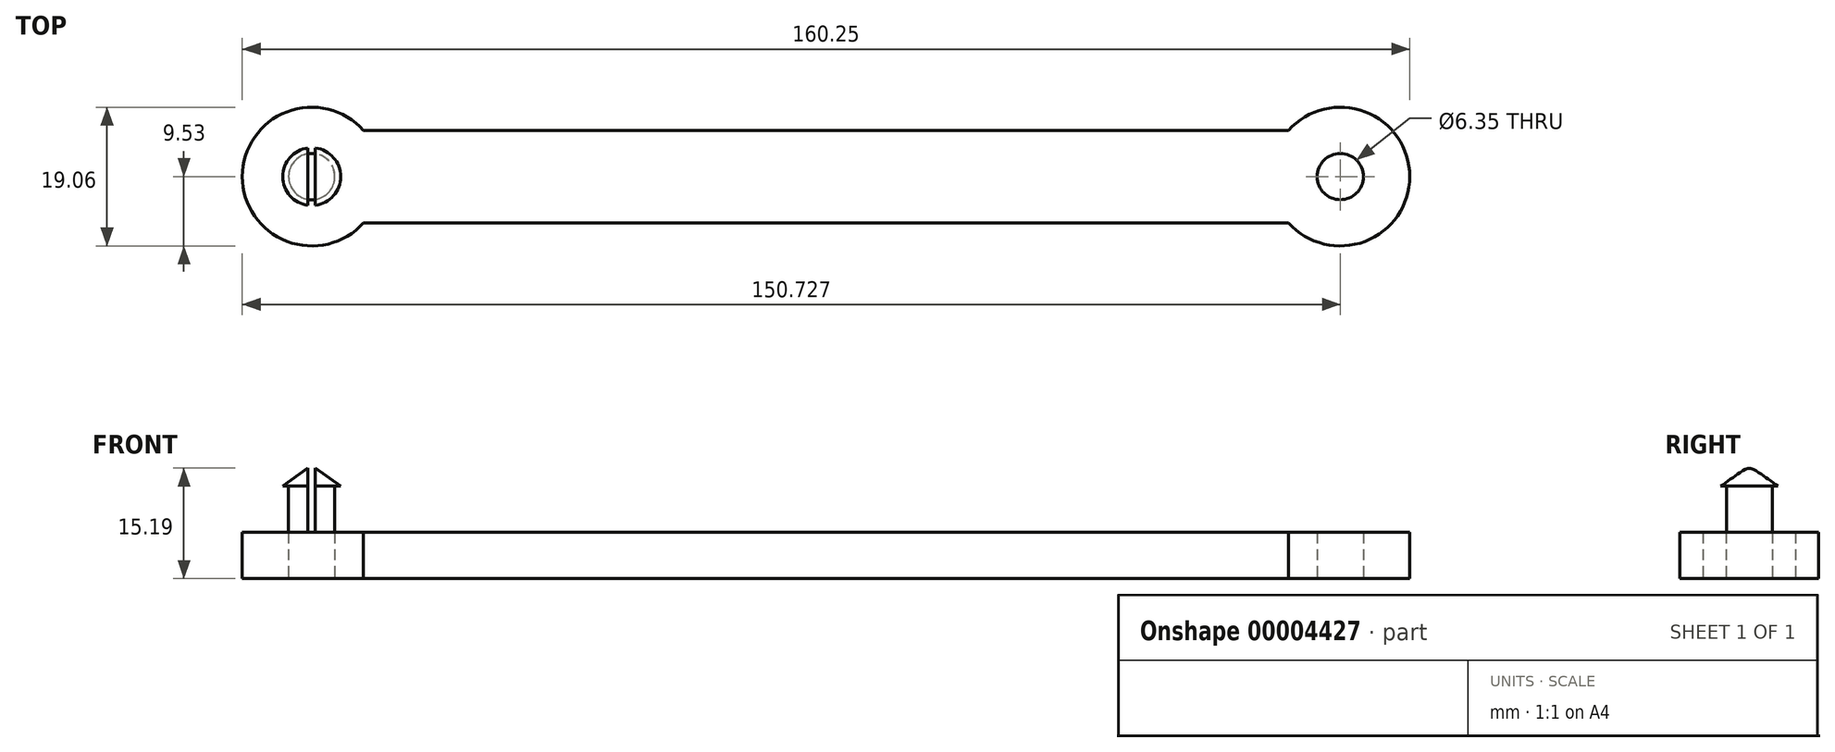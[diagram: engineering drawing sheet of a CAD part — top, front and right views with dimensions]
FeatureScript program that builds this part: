
annotation { "Feature Type Name" : "Feature", "Feature Type Description" : "" }
export const myFeature = defineFeature(function(context is Context, id is Id, definition is map)
    precondition{}
    {
        {
            var Q0;
            Q0=qCreatedBy(makeId("Top.planeOp"),FACE);
            var sketch = newSketch(context, id + "F0", { "sketchPlane" : qUnion([Q0])});
            skCircle(sketch, "E0", {"center": v(-76.63, 0) * mm, "radius": 9.53 * mm});
            skCircle(sketch, "E1", {"center": v(64.57, 0) * mm, "radius": 9.53 * mm});
            skLineSegment(sketch, "E2", {"start": v(-69.53, -6.35) * mm, "end": v(57.47, -6.35) * mm});
            skLineSegment(sketch, "E3", {"start": v(-69.53, 6.35) * mm, "end": v(57.47, 6.35) * mm});
            skCircle(sketch, "E4", {"center": v(64.57, 0) * mm, "radius": 3.18 * mm});
            skCircle(sketch, "E5", {"center": v(-76.63, 0) * mm, "radius": 3.18 * mm});
            skSolve(sketch);
        }
        {
            var Q0;
            Q0=makeQuery(id+"F0.imprint","IMPRINT",FACE,{"disambiguationData":[TD([[makeQuery(id+"F0.imprint","IMPRINT",EDGE,{"derivedFrom":sQuery(id+"F0.wireOp",EDGE,"E5")}),1.0]])]});
            var Q1;
            Q1=makeQuery(id+"F0.imprint","IMPRINT",FACE,{"disambiguationData":[TD([[makeQuery(id+"F0.imprint","IMPRINT",EDGE,{"derivedFrom":sQuery(id+"F0.wireOp",EDGE,"E4")}),-1.0]])]});
            var Q2;
            {var subQ1=sQuery(id+"F0.wireOp",EDGE,"E2");Q2=makeQuery(id+"F0.imprint","IMPRINT",FACE,{"disambiguationData":[TD([[makeQuery(id+"F0.imprint","IMPRINT",EDGE,{"derivedFrom":subQ1}),1.0]])]});}
            var Q3;
            Q3=makeQuery(id+"F0.imprint","IMPRINT",FACE,{"disambiguationData":[TD([[makeQuery(id+"F0.imprint","IMPRINT",EDGE,{"derivedFrom":sQuery(id+"F0.wireOp",EDGE,"E4")}),1.0]])]});
            var Q4;
            Q4=makeQuery(id+"F0.imprint","IMPRINT",FACE,{"disambiguationData":[TD([[makeQuery(id+"F0.imprint","IMPRINT",EDGE,{"derivedFrom":sQuery(id+"F0.wireOp",EDGE,"E5")}),-1.0]])]});
            extrude(context, id + "F1", {"entities" : qUnion([Q0, Q1, Q2, Q3, Q4]), "depth" : 6.35 * mm});
        }
        {
            var Q0;
            Q0=makeQuery(id+"F0.imprint","IMPRINT",FACE,{"disambiguationData":[TD([[makeQuery(id+"F0.imprint","IMPRINT",EDGE,{"derivedFrom":sQuery(id+"F0.wireOp",EDGE,"E5")}),1.0]])]});
            extrude(context, id + "F2", {"entities" : qUnion([Q0]), "depth" : 12.7 * mm});
        }
        {
            var Q0;
            Q0=makeQuery(id+"F0.imprint","IMPRINT",FACE,{"disambiguationData":[TD([[makeQuery(id+"F0.imprint","IMPRINT",EDGE,{"derivedFrom":sQuery(id+"F0.wireOp",EDGE,"E4")}),1.0]])]});
            extrude(context, id + "F3", {"entities" : qUnion([Q0]), "operationType" : NewBodyOperationType.REMOVE, "depth" : 6.35 * mm});
        }
        {
            var Q0;
            Q0=qCreatedBy(makeId("Front.planeOp"),FACE);
            var sketch = newSketch(context, id + "F4", { "sketchPlane" : qUnion([Q0])});
            skLineSegment(sketch, "E6", {"start": v(-76.63, 0) * mm, "end": v(-76.63, 0) * mm});
            skLineSegment(sketch, "E7", {"start": v(-72.66, 12.7) * mm, "end": v(-76.63, 12.7) * mm});
            skLineSegment(sketch, "E8", {"start": v(-76.63, 20.46) * mm, "end": v(-76.63, 0) * mm, "construction": true});
            skLineSegment(sketch, "E9", {"start": v(-72.66, 12.7) * mm, "end": v(-76.63, 15.56) * mm});
            skLineSegment(sketch, "E10", {"start": v(-76.63, 15.56) * mm, "end": v(-76.63, 12.7) * mm});
            skSolve(sketch);
        }
        {
            var Q0;
            Q0=makeQuery(id+"F4.imprint","IMPRINT",FACE,{"disambiguationData":[TD([[makeQuery(id+"F4.imprint","IMPRINT",EDGE,{"derivedFrom":sQuery(id+"F4.wireOp",EDGE,"E7")}),-1.0]])]});
            var Q1;
            Q1=sQuery(id+"F4.wireOp",EDGE,"E9");
            var Q2;
            Q2=sQuery(id+"F4.wireOp",EDGE,"E7");
            var Q3;
            Q3=sQuery(id+"F4.wireOp",EDGE,"E8");
            revolve(context, id + "F5", {"operationType" : NewBodyOperationType.ADD, "entities" : qUnion([Q0]), "surfaceEntities" : qUnion([Q1, Q2]), "axis" : qUnion([Q3]), "revolveType" : RevolveType.FULL});
        }
        {
            var Q0;
            Q0=qCreatedBy(makeId("Front.planeOp"),FACE);
            var sketch = newSketch(context, id + "F6", { "sketchPlane" : qUnion([Q0])});
            skLineSegment(sketch, "E11.bottom", {"start": v(-76.12, 15.56) * mm, "end": v(-77.14, 15.56) * mm});
            skLineSegment(sketch, "E11.top", {"start": v(-76.12, 6.35) * mm, "end": v(-77.14, 6.35) * mm});
            skLineSegment(sketch, "E11.left", {"start": v(-76.12, 15.56) * mm, "end": v(-76.12, 6.35) * mm});
            skLineSegment(sketch, "E11.right", {"start": v(-77.14, 15.56) * mm, "end": v(-77.14, 6.35) * mm});
            skSolve(sketch);
        }
        {
            var Q0;
            Q0 = qSketchRegion(id + "F6", true);
            extrude(context, id + "F7", {"entities" : qUnion([Q0]), "operationType" : NewBodyOperationType.REMOVE, "endBound" : BoundingType.SYMMETRIC, "oppositeDirection" : true, "depth" : 25.4 * mm});
        }
    });
